# Revit family: 3FGB_PN16_DN125_RFA_2019
name_source: partatom
category: Pipe Accessories
units: mm (PartAtom-declared; Revit-internal decimal feet)

## family parameters
Always vertical = Yes
Cut with Voids When Loaded = No
Part Type = Valve - Breaks Into
Round Connector Dimension = Use Diameter
Shared = No
Work Plane-Based = No

## types (5) — shared parameters
CAT = No
CAT0 = Yes
L2D_Min = 30 mm  [stored 0.0984252 ft]
MC = Yes
MT = 2
Manufacturer = Hydronix
QmdConnectorList = 301;D;302;D;303;D
R9 = 4 mm  [stored 0.0131234 ft]
Type Comments = Přírubový; EQM charakteristika ve směru A-AB; PN16; -10~+150°C
URL = www.hydronix.cz
X1 = 2 mm  [stored 0.00656168 ft]
Z10 = 5 mm  [stored 0.0164042 ft]
Z19 = 10 mm  [stored 0.0328084 ft]
Z4 = 12 mm  [stored 0.0393701 ft]
Z5 = 6 mm  [stored 0.019685 ft]
Z6 = 6 mm  [stored 0.019685 ft]
Z7 = 3 mm  [stored 0.00984252 ft]
Z8 = 6 mm  [stored 0.019685 ft]
Z9 = 4 mm  [stored 0.0131234 ft]
magiPartTypeId = 320

## per-type parameters (varying)
- 3FGB PN16 DN100: A1=133 mm; CenSd_R6_6=15 mm  [stored 0.0492126 ft]; D=100 mm; D2=69 mm; D3=81 mm; D4=69 mm; DT2=50 mm; Description=3 cestný regulační ventil přírubový; DN100; PN16; kvs130; zdvih 45mm; FD=220 mm; FDT2=110 mm; H1=176 mm; H2=45 mm; H3=117 mm; H4=175 mm; HCD=180 mm; HCDT2=77 mm; HD=18 mm  [stored 0.0590551 ft]; L=350 mm; L2D=350 mm; LT2=175 mm; MC Product Code=3FGB100 (DN100; PN16; kvs130); N=8; R1=46 mm; R10=7 mm; R11=10 mm  [stored 0.0328084 ft]; R12=5 mm  [stored 0.0164042 ft]; R13=55 mm; R2=57 mm; R3=31 mm; R4=25 mm  [stored 0.082021 ft]; R5=20 mm  [stored 0.0656168 ft]; R6=17 mm; R7=10 mm  [stored 0.0328084 ft]; R8=8 mm  [stored 0.0262467 ft]; W2D=100 mm; X2=17 mm; X2__ve=-17 mm; X3=28 mm; X4=17 mm; Y1=62 mm; Z11=72 mm; Z12=55 mm; Z13=8 mm  [stored 0.0262467 ft]; Z14=15 mm  [stored 0.0492126 ft]; Z14__ve=-15 mm; Z15=41 mm; Z16=11 mm; Z17=5 mm  [stored 0.0164042 ft]; Z18=29 mm; Z3=166 mm
- 3FGB PN16 DN125: A1=155 mm; CenSd_R6_6=17 mm; D=125 mm; D2=79 mm; D3=96 mm; D4=82 mm; DT2=63 mm; Description=3 cestný regulační ventil přírubový; DN125; PN16; kvs200; zdvih 45mm; FD=250 mm; FDT2=125 mm; H1=199 mm; H2=45 mm; H3=139 mm; H4=200 mm; HCD=210 mm; HCDT2=92 mm; HD=18 mm  [stored 0.0590551 ft]; L=400 mm; L2D=400 mm; LT2=200 mm; MC Product Code=3FGB125 (DN125; PN16; kvs200); N=8; R1=55 mm; R10=8 mm  [stored 0.0262467 ft]; R11=12 mm  [stored 0.0393701 ft]; R12=6 mm  [stored 0.019685 ft]; R13=66 mm; R2=69 mm; R3=36 mm; R4=29 mm; R5=23 mm; R6=19 mm; R7=12 mm  [stored 0.0393701 ft]; R8=9 mm; W2D=125 mm; X2=20 mm  [stored 0.0656168 ft]; X2__ve=-20 mm  [stored -0.0656168 ft]; X3=32 mm; X4=20 mm  [stored 0.0656168 ft]; Y1=71 mm; Z11=84 mm; Z12=63 mm; Z13=9 mm; Z14=17 mm; Z14__ve=-17 mm; Z15=49 mm; Z16=11 mm; Z17=5 mm  [stored 0.0164042 ft]; Z18=29 mm; Z3=194 mm
- 3FGB PN16 DN150: A1=181 mm; CenSd_R6_6=20 mm  [stored 0.0656168 ft]; D=150 mm; D2=95 mm; D3=109 mm; D4=93 mm; DT2=75 mm; Description=3 cestný regulační ventil přírubový; DN150; PN16; kvs300; zdvih 45mm; FD=285 mm; FDT2=143 mm; H1=217 mm; H2=45 mm; H3=157 mm; H4=240 mm; HCD=240 mm; HCDT2=104 mm; HD=22 mm  [stored 0.0721785 ft]; L=480 mm; L2D=480 mm; LT2=240 mm; MC Product Code=3FGB150 (DN150; PN16; kvs300); N=8; R1=62 mm; R10=9 mm; R11=14 mm  [stored 0.0459318 ft]; R12=7 mm; R13=75 mm; R2=78 mm; R3=43 mm; R4=34 mm; R5=27 mm; R6=23 mm; R7=14 mm  [stored 0.0459318 ft]; R8=10 mm  [stored 0.0328084 ft]; W2D=150 mm; X2=24 mm; X2__ve=-24 mm; X3=38 mm; X4=24 mm; Y1=86 mm; Z11=96 mm; Z12=76 mm; Z13=11 mm; Z14=20 mm  [stored 0.0656168 ft]; Z14__ve=-20 mm  [stored -0.0656168 ft]; Z15=55 mm; Z16=11 mm; Z17=5 mm  [stored 0.0164042 ft]; Z18=29 mm; Z3=226 mm
- 3FGB PN16 DN065: A1=109 mm; CenSd_R6_6=12 mm  [stored 0.0393701 ft]; D=65 mm; D2=57 mm; D3=64 mm; D4=54 mm; DT2=33 mm; Description=3 cestný regulační ventil přírubový; DN65; PN16; kvs63; zdvih 25mm; FD=185 mm; FDT2=93 mm; H1=155 mm; H2=25 mm  [stored 0.082021 ft]; H3=95 mm; H4=145 mm; HCD=145 mm; HCDT2=59 mm; HD=18 mm  [stored 0.0590551 ft]; L=290 mm; L2D=290 mm; LT2=145 mm; MC Product Code=3FGB65 (DN65; PN16; kvs63); N=4; R1=35 mm; R10=6 mm  [stored 0.019685 ft]; R11=8 mm  [stored 0.0262467 ft]; R12=4 mm  [stored 0.0131234 ft]; R13=42 mm; R2=44 mm; R3=26 mm; R4=21 mm; R5=16 mm; R6=14 mm  [stored 0.0459318 ft]; R7=8 mm  [stored 0.0262467 ft]; R8=6 mm  [stored 0.019685 ft]; W2D=65 mm; X2=14 mm  [stored 0.0459318 ft]; X2__ve=-14 mm; X3=23 mm; X4=14 mm  [stored 0.0459318 ft]; Y1=51 mm; Z11=58 mm; Z12=46 mm; Z13=7 mm; Z14=12 mm  [stored 0.0393701 ft]; Z14__ve=-12 mm; Z15=33 mm; Z16=6 mm  [stored 0.019685 ft]; Z17=3 mm  [stored 0.00984252 ft]; Z18=16 mm; Z3=137 mm
- 3FGB PN16 DN080: A1=119 mm; CenSd_R6_6=13 mm; D=80 mm; D2=61 mm; D3=71 mm; D4=60 mm; DT2=40 mm; Description=3 cestný regulační ventil přírubový; DN80; PN16; kvs100; zdvih 45mm; FD=200 mm; FDT2=100 mm; H1=165 mm; H2=45 mm; H3=105 mm; H4=155 mm; HCD=160 mm; HCDT2=67 mm; HD=18 mm  [stored 0.0590551 ft]; L=310 mm; L2D=310 mm; LT2=155 mm; MC Product Code=3FGB80 (DN80; PN16; kvs100); N=4; R1=40 mm; R10=6 mm  [stored 0.019685 ft]; R11=9 mm; R12=5 mm  [stored 0.0164042 ft]; R13=48 mm; R2=50 mm; R3=28 mm; R4=22 mm  [stored 0.0721785 ft]; R5=18 mm  [stored 0.0590551 ft]; R6=15 mm  [stored 0.0492126 ft]; R7=9 mm; R8=7 mm; W2D=80 mm; X2=15 mm  [stored 0.0492126 ft]; X2__ve=-15 mm; X3=24 mm; X4=15 mm  [stored 0.0492126 ft]; Y1=55 mm; Z11=64 mm; Z12=49 mm; Z13=7 mm; Z14=13 mm; Z14__ve=-13 mm; Z15=37 mm; Z16=11 mm; Z17=5 mm  [stored 0.0164042 ft]; Z18=29 mm; Z3=149 mm

note: [stored X ft] marks values corroborated as IEEE doubles in the binary element streams (Revit-internal decimal feet)

## geometry (parser evidence)
native form markers: Sweep x1
no freeform markers — native parametric forms only
